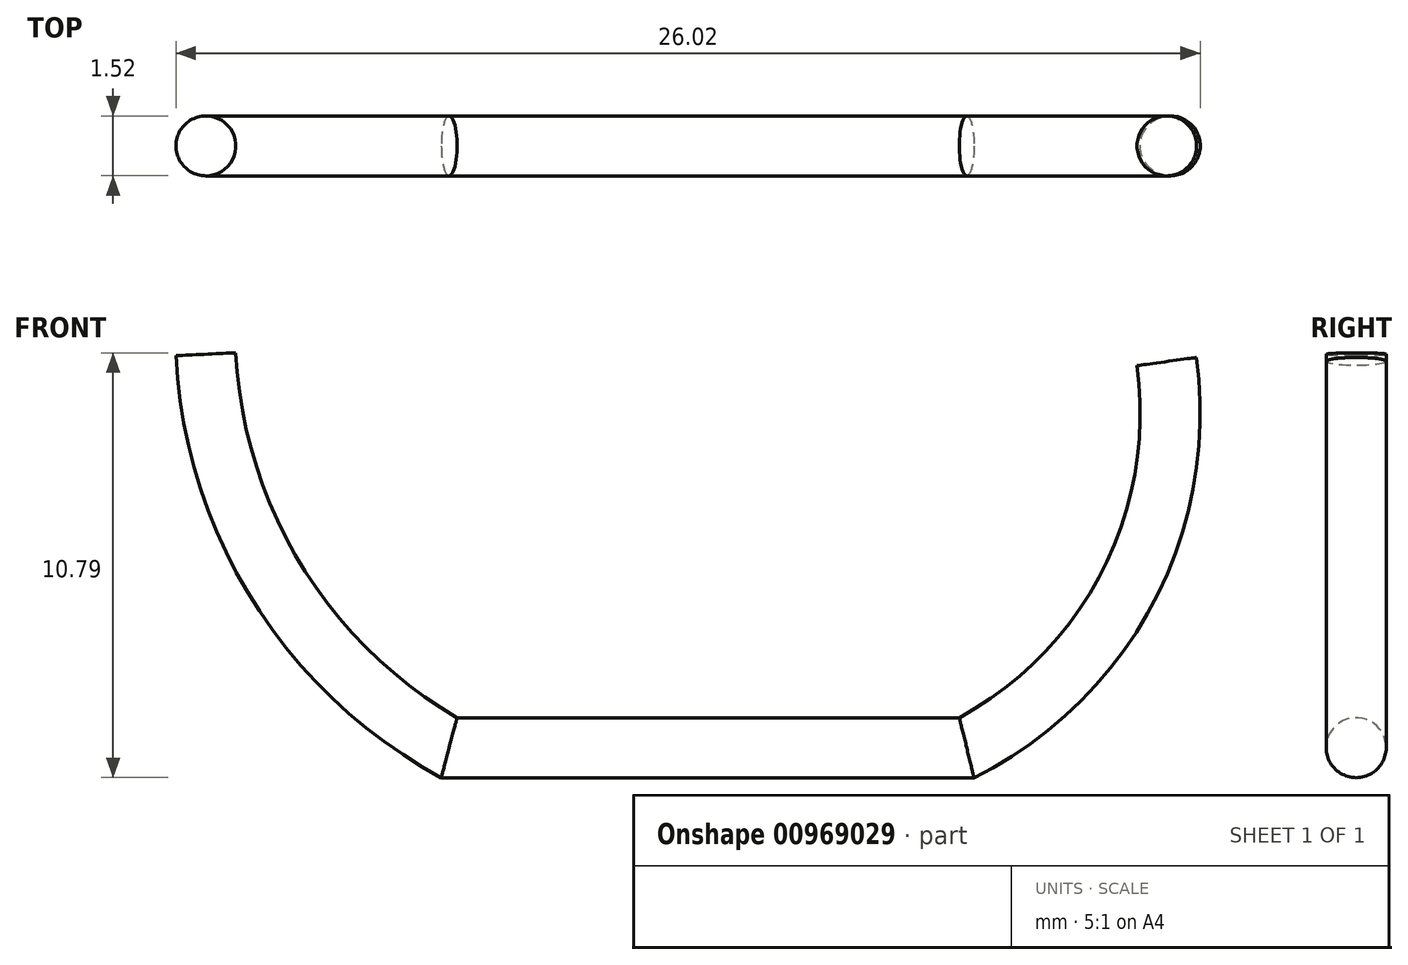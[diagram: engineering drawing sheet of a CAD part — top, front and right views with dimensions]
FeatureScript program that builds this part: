
annotation { "Feature Type Name" : "Feature", "Feature Type Description" : "" }
export const myFeature = defineFeature(function(context is Context, id is Id, definition is map)
    precondition{}
    {
        {
            var Q0;
            Q0=qCreatedBy(makeId("Right.planeOp"),FACE);
            var sketch = newSketch(context, id + "F0", { "sketchPlane" : qUnion([Q0])});
            skCircle(sketch, "E0", {"center": v(0, 0) * mm, "radius": 0.76 * mm});
            skSolve(sketch);
        }
        {
            var Q0;
            Q0=qCreatedBy(makeId("Front.planeOp"),FACE);
            var sketch = newSketch(context, id + "F1", { "sketchPlane" : qUnion([Q0])});
            skPoint(sketch, "E1.start.orphan", {"position": v(-6.42, 0) * mm});
            skLineSegment(sketch, "E2", {"start": v(0, 0) * mm, "end": v(-6.42, 0) * mm});
            skLineSegment(sketch, "E3", {"start": v(0, 0) * mm, "end": v(6.73, 0) * mm});
            skPoint(sketch, "E4.start.orphan", {"position": v(-17.18, 11.93) * mm});
            skPoint(sketch, "E5.end.orphan", {"position": v(11.53, 11.93) * mm});
            skArc(sketch, "E6", {"start": v(6.73, 0) * mm, "mid": v(10.83, 4.1) * mm, "end": v(11.8, 9.81) * mm});
            skArc(sketch, "E7", {"start": v(-12.6, 10) * mm, "mid": v(-10.8, 4.2) * mm, "end": v(-6.42, 0) * mm});
            skSolve(sketch);
        }
        {
            var Q0;
            Q0=makeQuery(id+"F0.imprint","IMPRINT",FACE,{"disambiguationData":[TD([[makeQuery(id+"F0.imprint","IMPRINT",EDGE,{"derivedFrom":sQuery(id+"F0.wireOp",EDGE,"E0")}),1.0]])]});
            var Q1;
            Q1=sQuery(id+"F1.wireOp",EDGE,"E2");
            var Q2;
            Q2=sQuery(id+"F1.wireOp",EDGE,"E7");
            var Q3;
            Q3=sQuery(id+"F1.wireOp",EDGE,"E3");
            var Q4;
            Q4=sQuery(id+"F1.wireOp",EDGE,"E6");
            sweep(context, id + "F2", {"profiles" : qUnion([Q0]), "path" : qUnion([Q1, Q2, Q3, Q4])});
        }
    });
